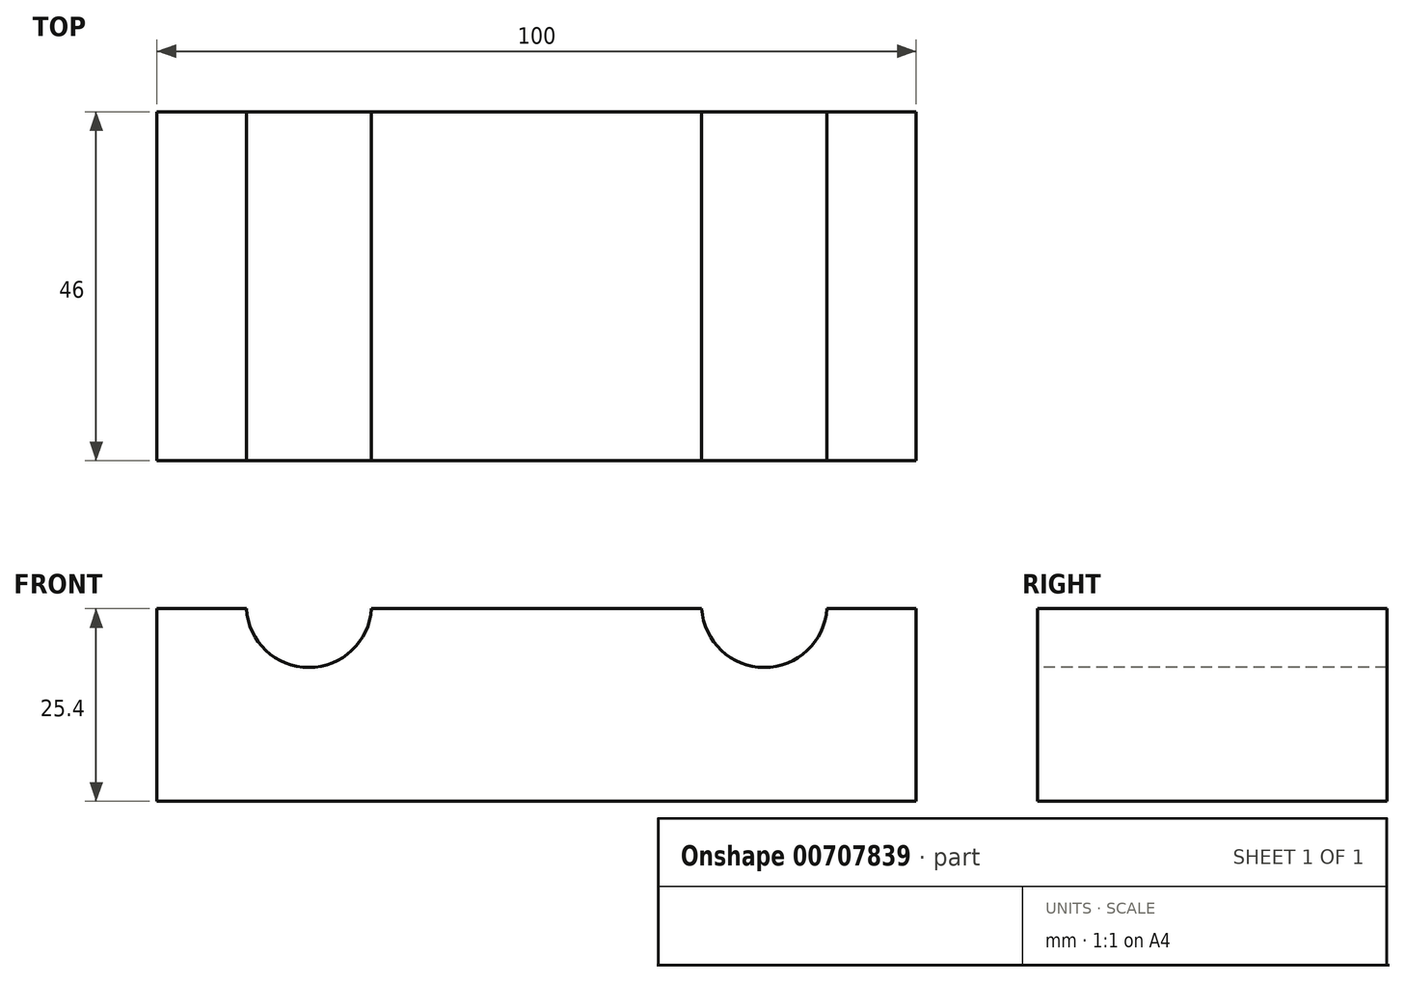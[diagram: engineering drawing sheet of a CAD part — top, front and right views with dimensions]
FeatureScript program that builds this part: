
annotation { "Feature Type Name" : "Feature", "Feature Type Description" : "" }
export const myFeature = defineFeature(function(context is Context, id is Id, definition is map)
    precondition{}
    {
        {
            var Q0;
            Q0=qCreatedBy(makeId("Top.planeOp"),FACE);
            var sketch = newSketch(context, id + "F0", { "sketchPlane" : qUnion([Q0])});
            skLineSegment(sketch, "E0.bottom", {"start": v(50, 23) * mm, "end": v(-50, 23) * mm});
            skLineSegment(sketch, "E0.top", {"start": v(50, -23) * mm, "end": v(-50, -23) * mm});
            skLineSegment(sketch, "E0.left", {"start": v(50, 23) * mm, "end": v(50, -23) * mm});
            skLineSegment(sketch, "E0.right", {"start": v(-50, 23) * mm, "end": v(-50, -23) * mm});
            skPoint(sketch, "E0.middle", {"position": v(0, 0) * mm});
            skSolve(sketch);
        }
        {
            var Q0;
            Q0=makeQuery(id+"F0.imprint","IMPRINT",FACE,{"disambiguationData":[TD([[makeQuery(id+"F0.imprint","IMPRINT",EDGE,{"derivedFrom":sQuery(id+"F0.wireOp",EDGE,"E0.bottom")}),1.0]])]});
            extrude(context, id + "F1", {"entities" : qUnion([Q0]), "depth" : 25.4 * mm, "offsetDistance" : 25.4 * mm});
        }
        {
            var Q0;
            Q0=qCreatedBy(makeId("Front.planeOp"),FACE);
            var sketch = newSketch(context, id + "F2", { "sketchPlane" : qUnion([Q0])});
            skCircle(sketch, "E1", {"center": v(-30, 25.9) * mm, "radius": 8.26 * mm});
            skCircle(sketch, "E2", {"center": v(30, 25.9) * mm, "radius": 8.26 * mm});
            skSolve(sketch);
        }
        {
            var Q0;
            Q0 = qSketchRegion(id + "F2", true);
            extrude(context, id + "F3", {"entities" : qUnion([Q0]), "operationType" : NewBodyOperationType.REMOVE, "endBound" : BoundingType.SYMMETRIC, "oppositeDirection" : true, "depth" : 254 * mm, "offsetDistance" : 25.4 * mm});
        }
    });
